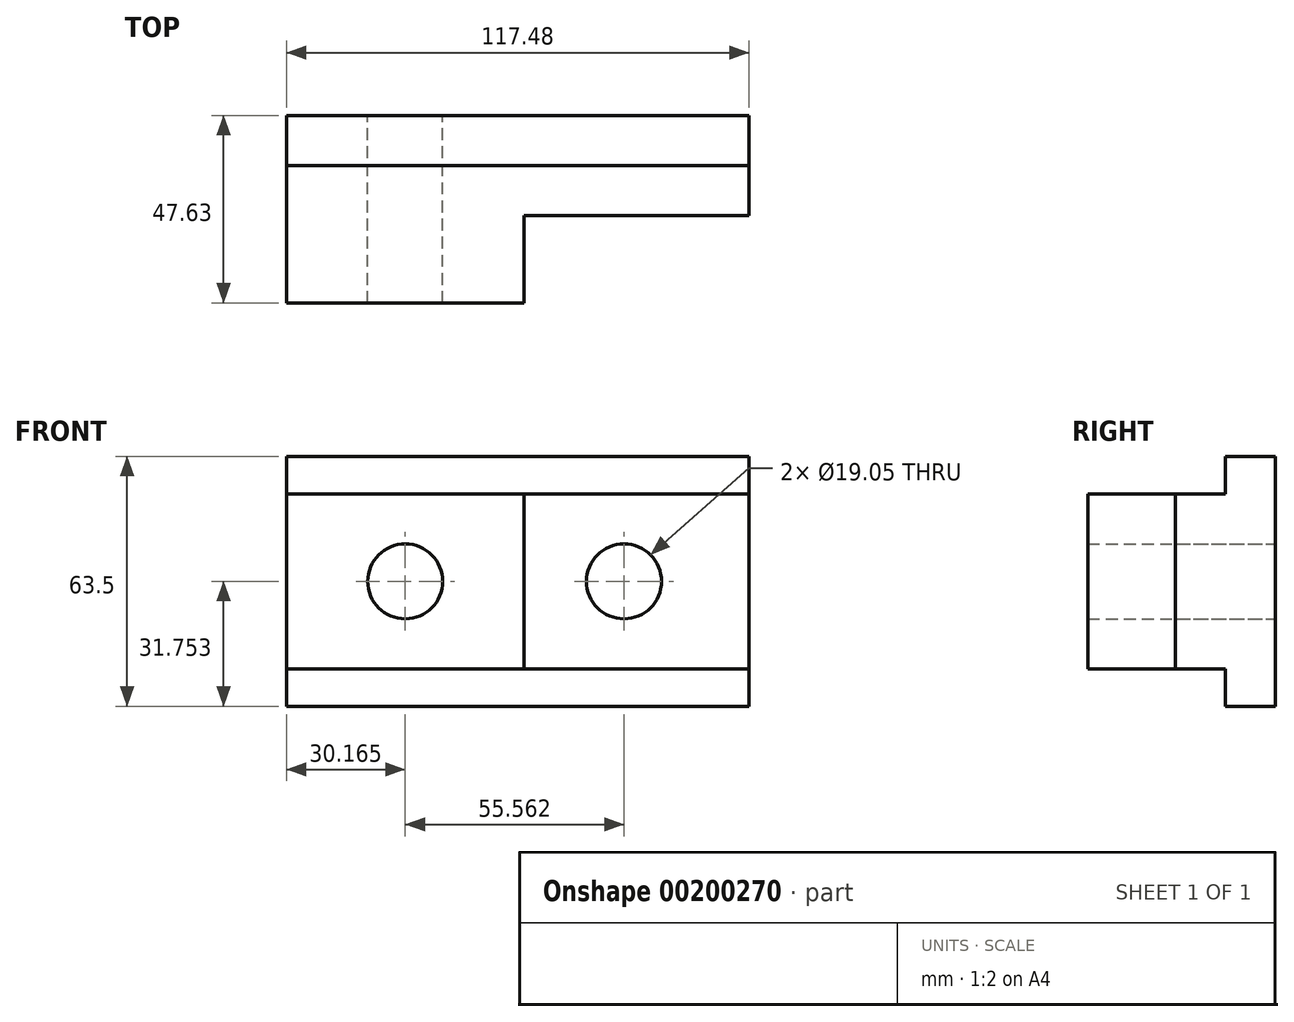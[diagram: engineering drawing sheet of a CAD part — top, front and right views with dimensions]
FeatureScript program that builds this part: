
annotation { "Feature Type Name" : "Feature", "Feature Type Description" : "" }
export const myFeature = defineFeature(function(context is Context, id is Id, definition is map)
    precondition{}
    {
        {
            var Q0;
            Q0=qCreatedBy(makeId("Front.planeOp"),FACE);
            var sketch = newSketch(context, id + "F0", { "sketchPlane" : qUnion([Q0])});
            skLineSegment(sketch, "E0.bottom", {"start": v(-58.74, 30.98) * mm, "end": v(58.74, 30.98) * mm});
            skLineSegment(sketch, "E0.top", {"start": v(-58.74, -32.52) * mm, "end": v(58.74, -32.52) * mm});
            skLineSegment(sketch, "E0.left", {"start": v(-58.74, 30.98) * mm, "end": v(-58.74, -32.52) * mm});
            skLineSegment(sketch, "E0.right", {"start": v(58.74, 30.98) * mm, "end": v(58.74, -32.52) * mm});
            skLineSegment(sketch, "E1", {"start": v(-58.74, -23) * mm, "end": v(58.74, -23) * mm});
            skLineSegment(sketch, "E2", {"start": v(-58.74, 21.46) * mm, "end": v(58.74, 21.46) * mm});
            skLineSegment(sketch, "E3", {"start": v(1.59, 21.46) * mm, "end": v(1.59, -23) * mm});
            skLineSegment(sketch, "E4", {"start": v(58.74, 21.46) * mm, "end": v(26.99, 21.46) * mm});
            skCircle(sketch, "E5", {"center": v(-28.58, -0.77) * mm, "radius": 9.53 * mm});
            skCircle(sketch, "E6", {"center": v(26.99, -0.77) * mm, "radius": 9.53 * mm});
            skPoint(sketch, "E7.orphan", {"position": v(-58.74, -0.77) * mm});
            skPoint(sketch, "E8.start.orphan", {"position": v(-28.58, 21.46) * mm});
            skPoint(sketch, "E9.trimOffspring.end.orphan", {"position": v(-28.58, -23) * mm});
            skPoint(sketch, "E10.orphan", {"position": v(26.99, -23) * mm});
            skSolve(sketch);
        }
        {
            var Q0;
            {var subQ0=sQuery(id+"F0.wireOp",EDGE,"E3");Q0=makeQuery(id+"F0.imprint","IMPRINT",FACE,{"disambiguationData":[TD([[makeQuery(id+"F0.imprint","IMPRINT",EDGE,{"derivedFrom":subQ0}),-1.0]])]});}
            extrude(context, id + "F1", {"entities" : qUnion([Q0]), "depth" : 47.62 * mm});
        }
        {
            var Q0;
            {var subQ0=sQuery(id+"F0.wireOp",EDGE,"E3");Q0=makeQuery(id+"F0.imprint","IMPRINT",FACE,{"disambiguationData":[TD([[makeQuery(id+"F0.imprint","IMPRINT",EDGE,{"derivedFrom":subQ0}),1.0]])]});}
            extrude(context, id + "F2", {"entities" : qUnion([Q0]), "operationType" : NewBodyOperationType.ADD, "depth" : 25.4 * mm});
        }
        {
            var Q0;
            {var subQ5=sQuery(id+"F0.wireOp",EDGE,"E0.bottom");Q0=makeQuery(id+"F0.imprint","IMPRINT",FACE,{"disambiguationData":[TD([[makeQuery(id+"F0.imprint","IMPRINT",EDGE,{"derivedFrom":subQ5}),-1.0]])]});}
            var Q1;
            {var subQ4=sQuery(id+"F0.wireOp",EDGE,"E0.top");Q1=makeQuery(id+"F0.imprint","IMPRINT",FACE,{"disambiguationData":[TD([[makeQuery(id+"F0.imprint","IMPRINT",EDGE,{"derivedFrom":subQ4}),1.0]])]});}
            extrude(context, id + "F3", {"entities" : qUnion([Q0, Q1]), "operationType" : NewBodyOperationType.ADD, "depth" : 12.7 * mm});
        }
    });
